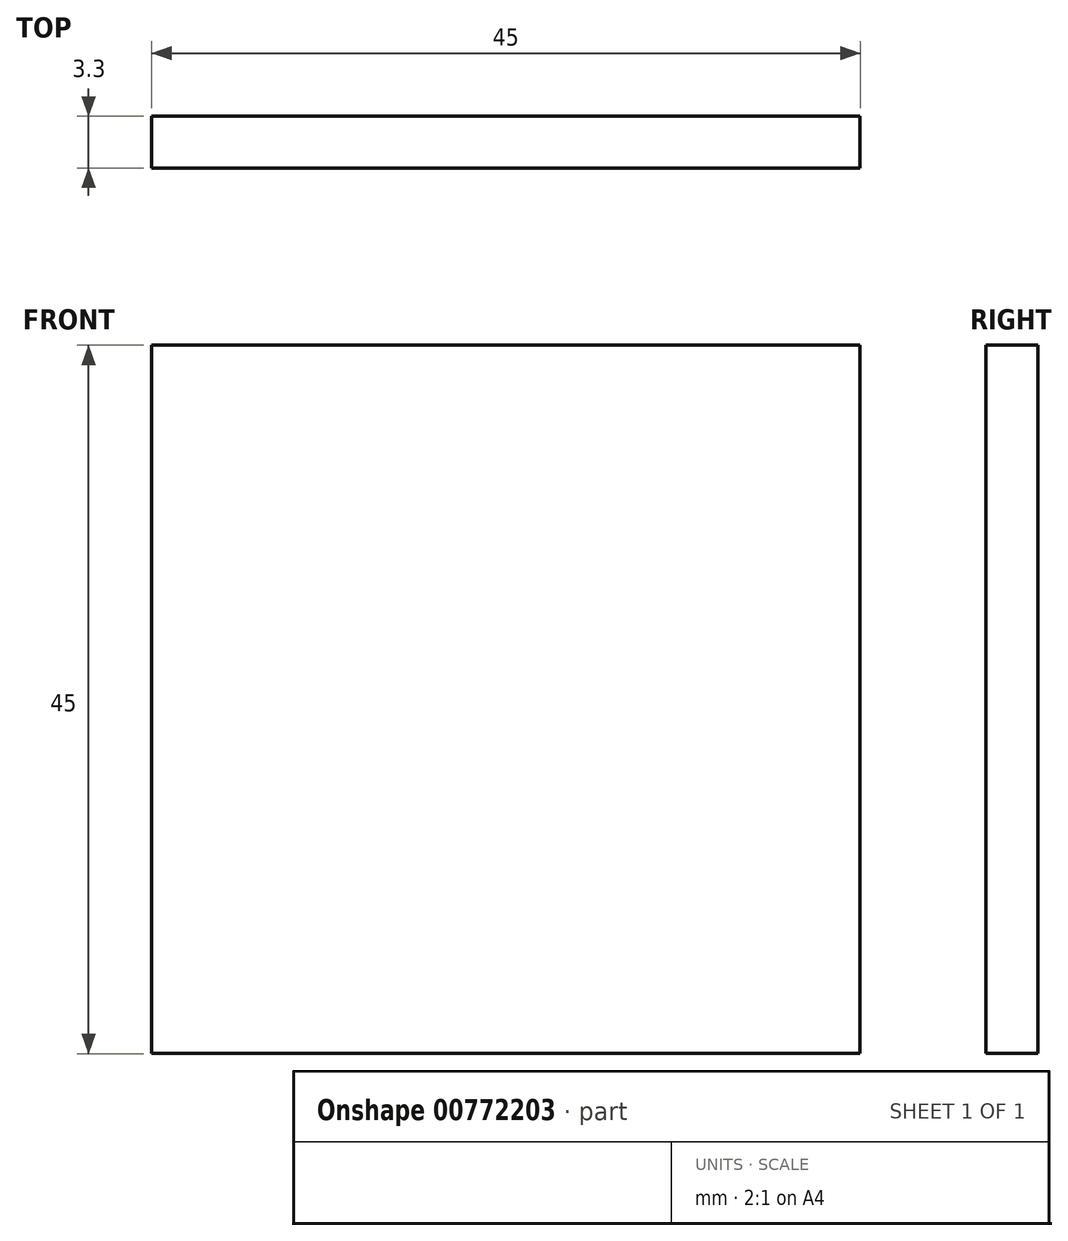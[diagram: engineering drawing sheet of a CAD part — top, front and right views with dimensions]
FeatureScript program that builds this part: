
annotation { "Feature Type Name" : "Feature", "Feature Type Description" : "" }
export const myFeature = defineFeature(function(context is Context, id is Id, definition is map)
    precondition{}
    {
        {
            var Q0;
            Q0=qCreatedBy(makeId("Front.planeOp"),FACE);
            var sketch = newSketch(context, id + "F0", { "sketchPlane" : qUnion([Q0])});
            skLineSegment(sketch, "E0.bottom", {"start": v(-22.47, -9.56) * mm, "end": v(22.53, -9.56) * mm});
            skLineSegment(sketch, "E0.top", {"start": v(-22.47, -54.56) * mm, "end": v(22.53, -54.56) * mm});
            skLineSegment(sketch, "E0.left", {"start": v(-22.47, -9.56) * mm, "end": v(-22.47, -54.56) * mm});
            skLineSegment(sketch, "E0.right", {"start": v(22.53, -9.56) * mm, "end": v(22.53, -54.56) * mm});
            skSolve(sketch);
        }
        {
            var Q0;
            Q0 = qSketchRegion(id + "F0", true);
            extrude(context, id + "F1", {"entities" : qUnion([Q0]), "depth" : 3.3 * mm, "offsetDistance" : 25 * mm});
        }
    });
